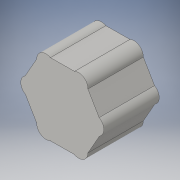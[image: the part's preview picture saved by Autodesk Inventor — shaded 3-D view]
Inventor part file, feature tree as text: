
AUTODESK INVENTOR PART (.ipt)
format: ipt  version: 2016 (Build 200138000, 138)  size: 114,688 bytes
history: native  units: in
note: dims shown in document units (in); Inventor stores cm internally (conversion verified against a paired STEP export)
features: extrude x1, sketch x1
ambient origin geometry x8: Origin, YZ Plane, XZ Plane, XY Plane, X Axis, Y Axis, Z Axis, Center Point
bodies: Solid1 (feature_tree)
feature tree (2):
  extrude  "Extrusion1"  Depth=0.6in TaperAngle=0.0deg
  sketch  "Sketch1"  dims[d6=0.78in d14=0.6in d15=0.0in]
